FCSTD DOCUMENT  (FreeCAD 0.14R3702 (Git))
Label: Tantillus-MakeSpace
License: CC-BY 3.0
LicenseURL: http://creativecommons.org/licenses/by/3.0/
objects: Mesh::Feature×43, Part::Cylinder×43, Part::Cut×35, Part::Feature×18, App::DocumentObjectGroup×17, Part::MultiFuse×16, Part::FeaturePython×15, PartDesign::Pad×12, PartDesign::Chamfer×9, Sketcher::SketchObject×8, PartDesign::Pocket×7, Part::Box×5, Part::Sweep×3, Part::Chamfer×2, PartDesign::Revolution×2, Part::Helix×1
note: 197 computed .brp shape members not serialized (recipe doc carries the construction recipe); baked Part::Feature solids carry a one-line shape summary decoded from their .brp

FEATURE [PartDesign::Pad] Pad  label="Pata001"
  Length = 335
  Length2 = 100
  Placement = pos=(-110,-110,-167.5) rot=(0,0,1;0rad)
  Type = 0
FEATURE [PartDesign::Pad] Pad001  label="Pata002"
  Length = 335
  Length2 = 100
  Placement = pos=(110,-110,-167.5) rot=(0,0,1;0rad)
  Type = 0
FEATURE [PartDesign::Pad] Pad002  label="Pata003"
  Length = 335
  Length2 = 100
  Placement = pos=(-110,110,-167.5) rot=(0,0,1;0rad)
  Type = 0
FEATURE [PartDesign::Pad] Pad003  label="Pata004"
  Length = 335
  Length2 = 100
  Placement = pos=(110,110,-167.5) rot=(0,0,1;0rad)
  Type = 0
FEATURE [PartDesign::Pad] Pad004  label="Trab001"
  Length = 200
  Length2 = 100
  Placement = pos=(-100,-110,-157.5) rot=(0,1,0;1.5708rad)
  Type = 0
FEATURE [Mesh::Feature] panel_combine_BOTTOM
  Placement = pos=(-125,-125,-182.5) rot=(0.57735,0.57735,0.57735;2.0944rad)
FEATURE [PartDesign::Pad] Pad005  label="Trab002"
  Length = 200
  Length2 = 100
  Placement = pos=(-110,-100,-157.5) rot=(0.57735,-0.57735,-0.57735;4.18879rad)
  Type = 0
FEATURE [Mesh::Feature] panel_combine_BOTTOM001
  Placement = pos=(-125,125,-182.5) rot=(1,0,0;1.5708rad)
FEATURE [Mesh::Feature] panel_combine_BOTTOM002
  Placement = pos=(125,-125,-182.5) rot=(0,0.707107,0.707107;3.14159rad)
FEATURE [Mesh::Feature] panel_combine_BOTTOM003
  Placement = pos=(125,125,-182.5) rot=(0.57735,-0.57735,-0.57735;2.0944rad)
FEATURE [PartDesign::Pad] Pad006  label="Trab003"
  Length = 200
  Length2 = 100
  Placement = pos=(110,-100,-157.5) rot=(0.57735,-0.57735,-0.57735;4.18879rad)
  Type = 0
FEATURE [PartDesign::Pad] Pad007  label="Trab004"
  Length = 200
  Length2 = 100
  Placement = pos=(-100,110,-157.5) rot=(0,1,0;1.5708rad)
  Type = 0
FEATURE [PartDesign::Pad] Pad008  label="Trab005"
  Length = 200
  Length2 = 100
  Placement = pos=(-100,-110,157.5) rot=(0,1,0;1.5708rad)
  Type = 0
FEATURE [PartDesign::Pad] Pad009  label="Trab006"
  Length = 200
  Length2 = 100
  Placement = pos=(-110,-100,157.5) rot=(0.57735,-0.57735,-0.57735;4.18879rad)
  Type = 0
FEATURE [PartDesign::Pad] Pad010  label="Trab007"
  Length = 200
  Length2 = 100
  Placement = pos=(110,-100,157.5) rot=(0.57735,-0.57735,-0.57735;4.18879rad)
  Type = 0
FEATURE [PartDesign::Pad] Pad011  label="Trab008"
  Length = 200
  Length2 = 100
  Placement = pos=(-100,110,157.5) rot=(0,1,0;1.5708rad)
  Type = 0
FEATURE [Mesh::Feature] AnguloFrontDerecho
  Placement = pos=(136,-60,165.5) rot=(0.707107,-0.707107,0;3.14159rad)
FEATURE [Mesh::Feature] AnguloFrontIzquierdo
  Placement = pos=(-33,-60.5,163.5) rot=(0.707107,-0.707107,0;3.14159rad)
FEATURE [Mesh::Feature] AnguloTraseroDerecho  label="AnguloTraseroDer"
  Placement = pos=(33,60,163.5) rot=(0.707107,0.707107,0;3.14159rad)
FEATURE [Mesh::Feature] AnguloTraseroIzq
  Placement = pos=(-52,130,163.5) rot=(0.707107,-0.707107,0;3.14159rad)
FEATURE [App::DocumentObjectGroup] Grupo001  label="AngulosSup"
  Group = -> [AnguloFrontDerecho,AnguloFrontIzquierdo,AnguloTraseroDerecho,AnguloTraseroIzq]
FEATURE [App::DocumentObjectGroup] Grupo002  label="AngulosInf"
  Group = -> [panel_combine_BOTTOM,panel_combine_BOTTOM001,panel_combine_BOTTOM002,panel_combine_BOTTOM003]
FEATURE [PartDesign::Chamfer] Chamfer001
  Placement = pos=(-124,-80.5,128) rot=(0,0,1;1.5708rad)
  Size = 0.25
FEATURE [PartDesign::Chamfer] Chamfer
  Placement = pos=(124,-80.5,128) rot=(0,0,1;1.5708rad)
  Size = 0.25
FEATURE [PartDesign::Chamfer] Chamfer002
  Placement = pos=(124,80.5,128) rot=(0,0,1;1.5708rad)
  Size = 0.25
FEATURE [PartDesign::Chamfer] Chamfer003
  Placement = pos=(-124,80.5,128) rot=(0,0,1;1.5708rad)
  Size = 0.25
FEATURE [App::DocumentObjectGroup] Grupo003  label="rodamientosY"
  Group = -> [Chamfer001,Chamfer,Chamfer002,Chamfer003]
FEATURE [PartDesign::Chamfer] Chamfer004
  Placement = pos=(80.5,-124,108) rot=(0,0,1;3.14159rad)
  Size = 0.25
FEATURE [PartDesign::Chamfer] Chamfer005
  Placement = pos=(80.5,124.5,108) rot=(0,0,1;3.14159rad)
  Size = 0.25
FEATURE [PartDesign::Chamfer] Chamfer006
  Placement = pos=(-81,124.5,108) rot=(0,0,1;3.14159rad)
  Size = 0.25
FEATURE [PartDesign::Chamfer] Chamfer007
  Placement = pos=(-81,-124,108) rot=(0,0,1;3.14159rad)
  Size = 0.25
FEATURE [App::DocumentObjectGroup] Grupo004  label="rodamientosX"
  Group = -> [Chamfer004,Chamfer005,Chamfer006,Chamfer007]
FEATURE [PartDesign::Pocket] Pocket006
  Length = 3
  Type = 0
FEATURE [Part::FeaturePython] refine  label="motor"  # WARN: FeaturePython — macro-defined, semantics opaque (R4)
  Base = -> Pocket006
  Placement = pos=(212,80.5,128) rot=(0,-1,0;1.5708rad)
FEATURE [Part::Cylinder] Cylinder  label="Cilindro"
  Angle = 360
  Height = 40
  Placement = pos=(0,0,0) rot=(0,1,0;1.5708rad)
  Radius = 2.5
FEATURE [Part::Cylinder] Cylinder001  label="Cilindro001"
  Angle = 360
  Height = 44
  Placement = pos=(-2,0,0) rot=(0,1,0;1.5708rad)
  Radius = 1.5
FEATURE [Part::Cut] Cut  label="soporte1"
  Base = -> Cylinder
  Placement = pos=(125,65,143.5) rot=(0,0,1;0rad)
  Tool = -> Cylinder001
FEATURE [Part::Cylinder] Cylinder002  label="Cilindro002"
  Angle = 360
  Height = 40
  Placement = pos=(0,0,0) rot=(0,1,0;1.5708rad)
  Radius = 2.5
FEATURE [Part::Cylinder] Cylinder003  label="Cilindro003"
  Angle = 360
  Height = 44
  Placement = pos=(-2,0,0) rot=(0,1,0;1.5708rad)
  Radius = 1.5
FEATURE [Part::Cut] Cut001  label="soporte2"
  Base = -> Cylinder002
  Placement = pos=(125,96,143.5) rot=(0,0,1;0rad)
  Tool = -> Cylinder003
FEATURE [Part::Cylinder] Cylinder004  label="Cilindro004"
  Angle = 360
  Height = 40
  Placement = pos=(0,0,0) rot=(0,1,0;1.5708rad)
  Radius = 2.5
FEATURE [Part::Cylinder] Cylinder005  label="Cilindro005"
  Angle = 360
  Height = 44
  Placement = pos=(-2,0,0) rot=(0,1,0;1.5708rad)
  Radius = 1.5
FEATURE [Part::Cut] Cut002  label="soporte3"
  Base = -> Cylinder004
  Placement = pos=(125,65,112.5) rot=(0,0,1;0rad)
  Tool = -> Cylinder005
FEATURE [Part::Cylinder] Cylinder006  label="Cilindro006"
  Angle = 360
  Height = 40
  Placement = pos=(0,0,0) rot=(0,1,0;1.5708rad)
  Radius = 2.5
FEATURE [Part::Cylinder] Cylinder007  label="Cilindro007"
  Angle = 360
  Height = 44
  Placement = pos=(-2,0,0) rot=(0,1,0;1.5708rad)
  Radius = 1.5
FEATURE [Part::Cut] Cut003  label="soporte4"
  Base = -> Cylinder006
  Placement = pos=(125,96,112.5) rot=(0,0,1;0rad)
  Tool = -> Cylinder007
FEATURE [Part::Cylinder] Cylinder008  label="barraM8Ymotor"
  Angle = 360
  Height = 276
  Placement = pos=(-81,-138,108) rot=(-0.57735,0.57735,0.57735;2.0944rad)
  Radius = 4
FEATURE [Mesh::Feature] Ruedecilla
  Placement = pos=(-147,68,133.8) rot=(0,1,0;1.5708rad)
FEATURE [Part::Cut] Cut004  label="soporte005"
  Base = -> Cylinder004
  Placement = pos=(-65.5,125,92.5) rot=(0,0,1;1.5708rad)
  Tool = -> Cylinder005
FEATURE [Part::Cut] Cut005  label="soporte006"
  Base = -> Cylinder002
  Placement = pos=(-96.5,125,123.5) rot=(0,0,1;1.5708rad)
  Tool = -> Cylinder003
FEATURE [Part::Cut] Cut006  label="soporte007"
  Base = -> Cylinder
  Placement = pos=(-65.5,125,123.5) rot=(0,0,1;1.5708rad)
  Tool = -> Cylinder001
FEATURE [Part::FeaturePython] refine001  label="motor001"  # WARN: FeaturePython — macro-defined, semantics opaque (R4)
  Base = -> Pocket006
  Placement = pos=(-81,212,108) rot=(0.57735,-0.57735,0.57735;2.0944rad)
FEATURE [Part::Cut] Cut007  label="soporte008"
  Base = -> Cylinder006
  Placement = pos=(-96.5,125,92.5) rot=(0,0,1;1.5708rad)
  Tool = -> Cylinder007
FEATURE [Mesh::Feature] Ruedecilla001
  Placement = pos=(-68.5,-147,113.7) rot=(0.57735,-0.57735,-0.57735;4.18879rad)
FEATURE [Part::Cylinder] Cylinder009  label="barraM8Xmotor"
  Angle = 360
  Height = 276
  Placement = pos=(138,-80.5,128) rot=(0.707107,0,-0.707107;3.14159rad)
  Radius = 4
FEATURE [Part::Cylinder] Cylinder010  label="barraM8Y"
  Angle = 360
  Height = 276
  Placement = pos=(80.5,-138,108) rot=(-0.57735,0.57735,0.57735;2.0944rad)
  Radius = 4
FEATURE [Mesh::Feature] Ruedecilla002
  Placement = pos=(-147,-93,133.7) rot=(0,1,0;1.5708rad)
FEATURE [Part::Cylinder] Cylinder011  label="barraM8X"
  Angle = 360
  Height = 276
  Placement = pos=(138,80.5,128) rot=(0.707107,0,-0.707107;3.14159rad)
  Radius = 4
FEATURE [Mesh::Feature] Ruedecilla003
  Placement = pos=(93,-147,113.7) rot=(0.57735,-0.57735,-0.57735;4.18879rad)
FEATURE [Mesh::Feature] Ruedecilla004
  Placement = pos=(147,-93,122.3) rot=(0,-1,0;1.5708rad)
FEATURE [Mesh::Feature] Ruedecilla005
  Placement = pos=(93,147,102.3) rot=(0.57735,-0.57735,0.57735;2.0944rad)
FEATURE [Mesh::Feature] printable_lm8uu_v  label="printable-lm8uu1"
  Placement = pos=(7.9,0.3,115.1) rot=(1,0,0;1.5708rad)
FEATURE [Mesh::Feature] printable_lm8uu_v001  label="printable-lm8uu2"
  Placement = pos=(2,16.2,128.6) rot=(0,1,0;1.5708rad)
FEATURE [Part::Cylinder] Cylinder012  label="barraX"
  Angle = 360
  Height = 175
  Placement = pos=(-88,10,127) rot=(0,1,0;1.5708rad)
  Radius = 4
FEATURE [Part::Cylinder] Cylinder013  label="barraY"
  Angle = 360
  Height = 175
  Placement = pos=(9.5,87.3,108.9) rot=(1,0,0;1.5708rad)
  Radius = 4
FEATURE [Mesh::Feature] XY_end_left
  Placement = pos=(161.5,-113,87.5) rot=(0.57735,-0.57735,-0.57735;4.18879rad)
FEATURE [Mesh::Feature] XY_end_right
  Placement = pos=(0,20,-4.5) rot=(0,0,1;1.5708rad)
FEATURE [Mesh::Feature] printable_lm8uu_v002  label="printable-lm8uu003"
  Placement = pos=(78.9,15,114.3) rot=(1,0,0;1.5708rad)
FEATURE [Mesh::Feature] printable_lm8uu_v003  label="printable-lm8uu004"
  Placement = pos=(-82.6,16,114.2) rot=(1,0,0;1.5708rad)
FEATURE [Mesh::Feature] printable_lm8uu_v004  label="printable-lm8uu005"
  Placement = pos=(15.5,-82.1,121.8) rot=(0.57735,0.57735,-0.57735;4.18879rad)
FEATURE [Mesh::Feature] printable_lm8uu_v005  label="printable-lm8uu006"
  Placement = pos=(14.5,78.9,121.7) rot=(0.57735,0.57735,-0.57735;4.18879rad)
FEATURE [Mesh::Feature] XY_end_right001
  Placement = pos=(19.5,0.5,240.5) rot=(1,0,0;3.14159rad)
FEATURE [Mesh::Feature] XY_end_left001
  Placement = pos=(-113.5,161.5,148.5) rot=(0.707107,0,0.707107;3.14159rad)
FEATURE [App::DocumentObjectGroup] Grupo010  label="estremos"
  Group = -> [XY_end_left,XY_end_right,printable_lm8uu_v002,printable_lm8uu_v003,printable_lm8uu_v004,printable_lm8uu_v005,XY_end_right001,XY_end_left001]
FEATURE [Part::Cylinder] Cylinder014  label="barraM8008"
  Angle = 360
  Height = 225
  Placement = pos=(-33,79.3,-133.5) rot=(0,0,1;0rad)
  Radius = 4
FEATURE [Part::Cylinder] Cylinder015  label="barraM8009"
  Angle = 360
  Height = 225
  Placement = pos=(37,79.3,-133.5) rot=(0,0,1;0rad)
  Radius = 4
FEATURE [Mesh::Feature] Z_lift
  Placement = pos=(107,253.5,219.1) rot=(0,0,1;1.5708rad)
FEATURE [Mesh::Feature] printable_lm8uu_v007  label="printable-lm8uu-v004"
  Placement = pos=(35.3,85.5,-3.9) rot=(0,0,1;0rad)
FEATURE [Mesh::Feature] printable_lm8uu_v008  label="printable-lm8uu-v005"
  Placement = pos=(-34.6,85.5,-3.9) rot=(0,0,1;0rad)
FEATURE [Part::Box] Box  label="tablelisa"
  Height = 3
  Length = 120
  Placement = pos=(53,45,161) rot=(0,0,1;0rad)
  Width = 120
FEATURE [Part::FeaturePython] refine002  label="motor002"  # WARN: FeaturePython — macro-defined, semantics opaque (R4)
  Placement = pos=(2,79,-180.5) rot=(0,0,1;0rad)
FEATURE [Part::Cylinder] Cylinder016  label="Cilindro008"
  Angle = 360
  Height = 10
  Placement = pos=(79.5,114.1,158) rot=(0,0,1;0rad)
  Radius = 2.6
FEATURE [Part::Cylinder] Cylinder017  label="Cilindro009"
  Angle = 360
  Height = 10
  Placement = pos=(144.5,114.1,158) rot=(0,0,1;0rad)
  Radius = 2.6
FEATURE [Part::Cylinder] Cylinder018  label="Cilindro010"
  Angle = 360
  Height = 10
  Placement = pos=(144.5,152.1,158) rot=(0,0,1;0rad)
  Radius = 2.6
FEATURE [Part::Cylinder] Cylinder019  label="Cilindro011"
  Angle = 360
  Height = 10
  Placement = pos=(79.5,152.1,158) rot=(0,0,1;0rad)
  Radius = 2.6
FEATURE [Part::Cut] Cut008
  Base = -> Box
  Tool = -> Cylinder016
FEATURE [Part::Cut] Cut009
  Base = -> Cut008
  Tool = -> Cylinder017
FEATURE [Part::Cut] Cut010
  Base = -> Cut009
  Tool = -> Cylinder019
FEATURE [Part::Cut] Cut011  label="mesainf01"
  Base = -> Cut010
  Tool = -> Cylinder018
FEATURE [Part::Box] Box001  label="tablelisa001"
  Height = 3
  Length = 120
  Placement = pos=(53,45,174) rot=(0,0,1;0rad)
  Width = 120
FEATURE [Sketcher::SketchObject] Sketch
  Placement = pos=(53,45,177) rot=(0,0,1;0rad)
  Support = -> Box001 [Face6]
  sketch-geometry (3):
    g0: Circle CenterX=5 CenterY=5 CenterZ=0 NormalX=0 NormalY=0 NormalZ=1 Radius=1.5
    g1: Circle CenterX=115 CenterY=5 CenterZ=0 NormalX=0 NormalY=0 NormalZ=1 Radius=1.5
    g2: Circle CenterX=60 CenterY=105 CenterZ=0 NormalX=0 NormalY=0 NormalZ=1 Radius=1.5
  constraints (9):
    c: Equal(g2,g1)
    c: Equal(g1,g0)
    c: Radius(g0) = 1.5
    c: DistanceY(g-1,g0) = 5
    c: DistanceX(g-1,g0) = 5
    c: DistanceY(g-1,g1) = 5
    c: DistanceX(g-1,g1) = 115
    c: DistanceY(g-1,g2) = 105
    c: DistanceX(g-1,g2) = 60
FEATURE [PartDesign::Pocket] Pocket  label="mesasup"
  Length = 5
  Placement = pos=(53,45,174) rot=(0,0,1;0rad)
  Sketch = -> Sketch
  Type = 1
FEATURE [Sketcher::SketchObject] Sketch001
  ExternalGeometry = -> [Cut011]
  Placement = pos=(0,0,164) rot=(0,0,1;0rad)
  Support = -> Cut011 [Face3]
  sketch-geometry (3):
    g0: Circle CenterX=58 CenterY=50 CenterZ=0 NormalX=0 NormalY=0 NormalZ=1 Radius=1.5
    g1: Circle CenterX=168 CenterY=50 CenterZ=0 NormalX=0 NormalY=0 NormalZ=1 Radius=1.5
    g2: Circle CenterX=113 CenterY=150 CenterZ=0 NormalX=0 NormalY=0 NormalZ=1 Radius=1.5
  constraints (9):
    c: Equal(g2,g1)
    c: Equal(g1,g0)
    c: Radius(g1) = 1.5
    c: DistanceX(g0,g-4) = -5
    c: DistanceY(g0,g-4) = -5
    c: DistanceX(g1,g-4) = 5
    c: DistanceY(g1,g-4) = -5
    c: DistanceX(g2,g-3) = -60
    c: DistanceY(g2,g-3) = 15
FEATURE [PartDesign::Pocket] Pocket007  label="mesainf"
  Length = 5
  Sketch = -> Sketch001
  Type = 1
FEATURE [Part::Cylinder] Cylinder020  label="Cilindro012"
  Angle = 360
  Height = 22
  Radius = 1.5
FEATURE [Part::Chamfer] Chamfer008
  Base = -> Cylinder020
  Edges = 1 edges r=0.2: [Edge3]
FEATURE [Part::Cylinder] Cylinder021  label="Cilindro013"
  Angle = 360
  Height = 3
  Placement = pos=(0,0,21) rot=(0,0,1;0rad)
  Radius = 2
FEATURE [Part::Chamfer] Chamfer009
  Base = -> Cylinder021
  Edges = 1 edges r=0.2: [Edge1]
FEATURE [Part::MultiFuse] Fusion
  Shapes = -> [Chamfer008,Chamfer009]
FEATURE [Sketcher::SketchObject] Sketch002
  Placement = pos=(0,0,24) rot=(0,0,1;0rad)
  Support = -> Fusion [Face7]
  sketch-geometry (7):
    g0: LineSegment StartX=-1.25 StartY=0.721688 StartZ=0 EndX=0 EndY=1.44338 EndZ=0
    g1: LineSegment StartX=0 StartY=1.44338 StartZ=0 EndX=1.25 EndY=0.721688 EndZ=0
    g2: LineSegment StartX=1.25 StartY=0.721688 StartZ=0 EndX=1.25 EndY=-0.721688 EndZ=0
    g3: LineSegment StartX=1.25 StartY=-0.721688 StartZ=0 EndX=0 EndY=-1.44338 EndZ=0
    g4: LineSegment StartX=0 StartY=-1.44338 StartZ=0 EndX=-1.25 EndY=-0.721688 EndZ=0
    g5: LineSegment StartX=-1.25 StartY=-0.721688 StartZ=0 EndX=-1.25 EndY=0.721688 EndZ=0
    g6: LineSegment [constr] StartX=0 StartY=1.44338 StartZ=0 EndX=0 EndY=0 EndZ=0
  constraints (20):
    c: PointOnObject(g0,g-2)
    c: Coincident(g0,g1)
    c: Coincident(g1,g2)
    c: Vertical(g2)
    c: Coincident(g2,g3)
    c: PointOnObject(g3,g-2)
    c: Coincident(g3,g4)
    c: Coincident(g4,g5)
    c: Coincident(g5,g0)
    c: Vertical(g5)
    c: Equal(g5,g0)
    c: Equal(g0,g1)
    c: Equal(g1,g2)
    c: Equal(g2,g3)
    c: Equal(g3,g4)
    c: Coincident(g6,g0)
    c: Coincident(g6,g-1)
    c: Angle(g0,g6) = 1.0472
    c: Symmetric(g0,g3,g-1)
    c: DistanceX(g2,g4) = -2.5
FEATURE [PartDesign::Pocket] Pocket008
  Length = 2
  Sketch = -> Sketch002
  Type = 0
FEATURE [Part::Cylinder] Cylinder022  label="Cilindro014"
  Angle = 360
  Height = 0.3
  Placement = pos=(0,0,20.7) rot=(0,0,1;0rad)
  Radius = 3
FEATURE [Part::MultiFuse] Fusion001
  Shapes = -> [Cylinder022,Pocket008]
FEATURE [Part::Cylinder] Cylinder023  label="Cilindro015"
  Angle = 360
  Height = 0.3
  Placement = pos=(0,0,17.4) rot=(0,0,1;0rad)
  Radius = 3
FEATURE [Part::MultiFuse] Fusion002
  Shapes = -> [Cylinder023,Fusion001]
FEATURE [Part::Cylinder] Cylinder024  label="Cilindro016"
  Angle = 360
  Height = 0.3
  Placement = pos=(0,0,7.7) rot=(0,0,1;0rad)
  Radius = 3
FEATURE [Part::MultiFuse] Fusion003
  Shapes = -> [Cylinder024,Fusion002]
FEATURE [Part::Cylinder] Cylinder025  label="Cilindro017"
  Angle = 360
  Height = 0.3
  Placement = pos=(0,0,4.4) rot=(0,0,1;0rad)
  Radius = 3
FEATURE [Part::MultiFuse] Fusion004
  Shapes = -> [Fusion003,Cylinder025]
FEATURE [Part::Helix] Helix  label="Muelletrazo"
  Angle = 0
  Height = 9.4
  LocalCoord = 0
  Pitch = 1
  Placement = pos=(0,0,8) rot=(0,0,1;0rad)
  Radius = 2.5
  Style = 1
FEATURE [Sketcher::SketchObject] Sketch003
  Placement = pos=(0,0,0) rot=(1,0,0;1.5708rad)
  sketch-geometry (1):
    g0: Circle CenterX=2.5 CenterY=8 CenterZ=0 NormalX=0 NormalY=0 NormalZ=1 Radius=0.1
  constraints (3):
    c: Radius(g0) = 0.1
    c: DistanceX(g-1,g0) = 2.5
    c: DistanceY(g-1,g0) = 8
FEATURE [Part::Sweep] Sweep
  Frenet = true
  Sections = -> [Sketch003]
  Solid = true
  Spine = -> Helix [Edge1]
  Transition = 1
FEATURE [Part::MultiFuse] Fusion005  label="tonillocama"
  Placement = pos=(-52,-59,-11) rot=(0,0,1;0rad)
  Shapes = -> [Fusion004,Sweep]
FEATURE [Part::Sweep] Sweep001
  Frenet = true
  Sections = -> [Sketch003]
  Solid = true
  Spine = -> Helix [Edge1]
  Transition = 1
FEATURE [Part::MultiFuse] Fusion006
  Shapes = -> [Fusion003,Cylinder025]
FEATURE [Part::MultiFuse] Fusion007  label="tonillocama001"
  Placement = pos=(58,-59,-11) rot=(0,0,1;0rad)
  Shapes = -> [Fusion006,Sweep001]
FEATURE [Part::MultiFuse] Fusion008
  Shapes = -> [Fusion003,Cylinder025]
FEATURE [Part::Sweep] Sweep002
  Frenet = true
  Sections = -> [Sketch003]
  Solid = true
  Spine = -> Helix [Edge1]
  Transition = 1
FEATURE [Part::MultiFuse] Fusion009  label="tonillocama002"
  Placement = pos=(3,41,-11) rot=(0,0,1;0rad)
  Shapes = -> [Fusion008,Sweep002]
FEATURE [Part::Cylinder] Cylinder026  label="Cilindro018"
  Angle = 360
  Height = 3
  Radius = 7
FEATURE [Sketcher::SketchObject] Sketch004  label="PasoTuerca"
  Placement = pos=(0,0,3) rot=(0,0,1;0rad)
  Support = -> Cylinder026 [Face2]
  sketch-geometry (8):
    g0: LineSegment StartX=-3.46409 StartY=0 StartZ=0 EndX=-1.73205 EndY=3 EndZ=0
    g1: LineSegment StartX=-1.73205 StartY=3 StartZ=0 EndX=1.73205 EndY=3 EndZ=0
    g2: LineSegment StartX=1.73205 StartY=3 StartZ=0 EndX=3.46409 EndY=0 EndZ=0
    g3: LineSegment StartX=3.46409 StartY=0 StartZ=0 EndX=1.73205 EndY=-3 EndZ=0
    g4: LineSegment StartX=1.73205 StartY=-3 StartZ=0 EndX=-1.73205 EndY=-3 EndZ=0
    g5: LineSegment StartX=-1.73205 StartY=-3 StartZ=0 EndX=-3.46409 EndY=0 EndZ=0
    g6: LineSegment [constr] StartX=-3.46409 StartY=0 StartZ=0 EndX=0 EndY=0 EndZ=0
    g7: LineSegment [constr] StartX=-1.73205 StartY=3 StartZ=0 EndX=0 EndY=0 EndZ=0
  constraints (21):
    c: Coincident(g0,g1)
    c: Coincident(g1,g2)
    c: Coincident(g2,g3)
    c: Coincident(g3,g4)
    c: Coincident(g4,g5)
    c: Coincident(g5,g0)
    c: Equal(g5,g0)
    c: Equal(g0,g1)
    c: Equal(g1,g2)
    c: Equal(g2,g3)
    c: Equal(g3,g4)
    c: Coincident(g6,g0)
    c: Horizontal(g1)
    c: Horizontal(g4)
    c: DistanceY(g0,g4) = -6
    c: Symmetric(g4,g0,g6)
    c: Symmetric(g0,g2,g6)
    c: Coincident(g7,g0)
    c: Coincident(g7,g6)
    c: Angle(g7,g6) = 1.0472
    c: Coincident(g6,g-1)
FEATURE [PartDesign::Pocket] Pocket009
  Length = 2
  Sketch = -> Sketch004
  Type = 0
FEATURE [PartDesign::Chamfer] Chamfer010
  Base = -> Pocket009 [Edge1]
  Size = 1
FEATURE [Part::Cylinder] Cylinder027  label="Cilindro019"
  Angle = 360
  Height = 10
  Placement = pos=(0,0,-2) rot=(0,0,1;0rad)
  Radius = 1.5
FEATURE [Part::Cut] Cut012
  Base = -> Chamfer010
  Tool = -> Cylinder027
FEATURE [Part::Cylinder] Cylinder028  label="Cilindro020"
  Angle = 360
  Height = 10
  Placement = pos=(7,0,-2) rot=(0,0,1;0rad)
  Radius = 1
FEATURE [Part::FeaturePython] Array  # Draft array (typed FeaturePython)
  Angle = 360
  ArrayType = 1
  Axis = (0,0,1)
  Base = -> Cylinder028
  Center = (0,0,0)
  IntervalX = (1,0,0)
  IntervalY = (0,1,0)
  IntervalZ = (0,0,1)
  NumberPolar = 12
  NumberX = 2
  NumberY = 2
  NumberZ = 1
FEATURE [Part::Cut] Cut013
  Base = -> Cut012
  Placement = pos=(-52,-59,-10.3) rot=(0,0,1;0rad)
  Tool = -> Array
FEATURE [Part::Cut] Cut014
  Base = -> Chamfer010
  Tool = -> Cylinder027
FEATURE [Part::FeaturePython] Array001  # Draft array (typed FeaturePython)
  Angle = 360
  ArrayType = 1
  Axis = (0,0,1)
  Base = -> Cylinder028
  Center = (0,0,0)
  IntervalX = (1,0,0)
  IntervalY = (0,1,0)
  IntervalZ = (0,0,1)
  NumberPolar = 12
  NumberX = 2
  NumberY = 2
  NumberZ = 1
FEATURE [Part::Cut] Cut015
  Base = -> Cut014
  Placement = pos=(58,-59,-10.3) rot=(0,0,1;0rad)
  Tool = -> Array001
FEATURE [Part::Cut] Cut016
  Base = -> Chamfer010
  Tool = -> Cylinder027
FEATURE [Part::FeaturePython] Array002  # Draft array (typed FeaturePython)
  Angle = 360
  ArrayType = 1
  Axis = (0,0,1)
  Base = -> Cylinder028
  Center = (0,0,0)
  IntervalX = (1,0,0)
  IntervalY = (0,1,0)
  IntervalZ = (0,0,1)
  NumberPolar = 12
  NumberX = 2
  NumberY = 2
  NumberZ = 1
FEATURE [Part::Cut] Cut017
  Base = -> Cut016
  Placement = pos=(3,41,-10.3) rot=(0,0,1;0rad)
  Tool = -> Array002
FEATURE [Part::Box] Box002  label="metraquilato"
  Height = 5
  Length = 125
  Placement = pos=(-59.5,-66.5,9.8) rot=(0,0,1;0rad)
  Width = 125
FEATURE [Part::Cylinder] Cylinder029  label="Cilindro021"
  Angle = 360
  Height = 40
  Radius = 8
FEATURE [Part::Cylinder] Cylinder030  label="Cilindro022"
  Angle = 360
  Height = 4.6
  Radius = 8
FEATURE [Part::Cylinder] Cylinder031  label="Cilindro023"
  Angle = 360
  Height = 10
  Placement = pos=(0,0,-2) rot=(0,0,1;0rad)
  Radius = 6
FEATURE [Part::Cut] Cut018
  Base = -> Cylinder030
  Placement = pos=(0,0,30.6) rot=(0,0,1;0rad)
  Tool = -> Cylinder031
FEATURE [Part::Cut] Cut019
  Base = -> Cylinder029
  Tool = -> Cut018
FEATURE [Part::Cylinder] Cylinder032  label="Cilindro024"
  Angle = 360
  Height = 42
  Placement = pos=(0,0,-1) rot=(0,0,1;0rad)
  Radius = 3.25
FEATURE [Part::Cut] Cut020
  Base = -> Cut019
  Tool = -> Cylinder032
FEATURE [Part::Cylinder] Cylinder033  label="Cilindro025"
  Angle = 360
  Height = 4.2
  Placement = pos=(0,0,-1) rot=(0,0,1;0rad)
  Radius = 4
FEATURE [Sketcher::SketchObject] Sketch005
  Placement = pos=(0,0,0) rot=(1,0,0;1.5708rad)
  sketch-geometry (4):
    g0: LineSegment [constr] StartX=-5 StartY=0 StartZ=0 EndX=5 EndY=0 EndZ=0
    g1: LineSegment StartX=-11.6906 StartY=3.86281 StartZ=0 EndX=-1.29847 EndY=-2.13708 EndZ=0
    g2: LineSegment StartX=-11.6906 StartY=-2.13708 StartZ=0 EndX=-11.6906 EndY=3.86281 EndZ=0
    g3: LineSegment StartX=-11.6906 StartY=-2.13708 StartZ=0 EndX=-1.29847 EndY=-2.13708 EndZ=0
  constraints (11):
    c: PointOnObject(g0,g-1)
    c: PointOnObject(g0,g-1)
    c: DistanceX(g0,g0) = -10
    c: Coincident(g2,g1)
    c: Vertical(g2)
    c: PointOnObject(g0,g1)
    c: Symmetric(g0,g0,g-2)
    c: Coincident(g3,g2)
    c: Coincident(g3,g1)
    c: Horizontal(g3)
    c: Angle(g0,g1) = 2.61799
FEATURE [Part::Cut] Cut021
  Base = -> Cut020
  Tool = -> Cylinder033
FEATURE [PartDesign::Revolution] Revolution
  Angle = 360
  Axis = (0,0,1)
  Base = (0,0,0)
  Placement = pos=(0,0,0) rot=(1,0,0;1.5708rad)
  ReferenceAxis = -> Sketch005 [V_Axis]
  Sketch = -> Sketch005
FEATURE [Part::Cut] Cut022
  Base = -> Cut021
  Tool = -> Revolution
FEATURE [Part::Cylinder] Cylinder034  label="Cilindro026"
  Angle = 360
  Height = 10
  Placement = pos=(4.2,0,0) rot=(0,1,0;1.5708rad)
  Radius = 1
FEATURE [Part::Cylinder] Cylinder035  label="Cilindro027"
  Angle = 360
  Height = 2
  Placement = pos=(0,0,-1) rot=(0,0,1;0rad)
  Radius = 4.2
FEATURE [Part::Cylinder] Cylinder036  label="Cilindro028"
  Angle = 60
  Height = 2
  Placement = pos=(0,0,-1) rot=(0,0,1;0rad)
  Radius = 14.2
FEATURE [Part::Cut] Cut023
  Base = -> Cylinder036
  Tool = -> Cylinder035
FEATURE [Part::Cylinder] Cylinder037  label="Cilindro029"
  Angle = 360
  Height = 10
  Placement = pos=(2.1,3.63731,0) rot=(-0.447214,0.774597,0.447214;1.82348rad)
  Radius = 1
FEATURE [Part::MultiFuse] Fusion010
  Shapes = -> [Cylinder034,Cut023]
FEATURE [Part::MultiFuse] Fusion011
  Shapes = -> [Cylinder037,Fusion010]
FEATURE [Part::FeaturePython] Array003  # Draft array (typed FeaturePython)
  Angle = 360
  ArrayType = 1
  Axis = (0,0,1)
  Base = -> Fusion011
  Center = (0,0,0)
  IntervalX = (1,0,0)
  IntervalY = (0,1,0)
  IntervalZ = (0,0,1)
  NumberPolar = 4
  NumberX = 1
  NumberY = 1
  NumberZ = 1
  Placement = pos=(0,0,13.5) rot=(0,0,1;0.261799rad)
FEATURE [Part::MultiFuse] Fusion012
  Shapes = -> [Cylinder037,Fusion010]
FEATURE [Part::FeaturePython] Array004  # Draft array (typed FeaturePython)
  Angle = 360
  ArrayType = 1
  Axis = (0,0,1)
  Base = -> Fusion012
  Center = (0,0,0)
  IntervalX = (1,0,0)
  IntervalY = (0,1,0)
  IntervalZ = (0,0,1)
  NumberPolar = 4
  NumberX = 1
  NumberY = 1
  NumberZ = 1
  Placement = pos=(0,0,16.5) rot=(0,0,1;0.261799rad)
FEATURE [Part::FeaturePython] Array005  # Draft array (typed FeaturePython)
  Angle = 360
  ArrayType = 1
  Axis = (0,0,1)
  Base = -> Fusion011
  Center = (0,0,0)
  IntervalX = (1,0,0)
  IntervalY = (0,1,0)
  IntervalZ = (0,0,1)
  NumberPolar = 4
  NumberX = 1
  NumberY = 1
  NumberZ = 1
  Placement = pos=(0,0,22.5) rot=(0,0,1;0.261799rad)
FEATURE [Part::MultiFuse] Fusion013
  Shapes = -> [Cylinder037,Fusion010]
FEATURE [Part::FeaturePython] Array006  # Draft array (typed FeaturePython)
  Angle = 360
  ArrayType = 1
  Axis = (0,0,1)
  Base = -> Fusion013
  Center = (0,0,0)
  IntervalX = (1,0,0)
  IntervalY = (0,1,0)
  IntervalZ = (0,0,1)
  NumberPolar = 4
  NumberX = 1
  NumberY = 1
  NumberZ = 1
  Placement = pos=(0,0,19.5) rot=(0,0,1;0.261799rad)
FEATURE [Part::MultiFuse] Fusion014
  Shapes = -> [Cylinder037,Fusion010]
FEATURE [Part::FeaturePython] Array007  # Draft array (typed FeaturePython)
  Angle = 360
  ArrayType = 1
  Axis = (0,0,1)
  Base = -> Fusion014
  Center = (0,0,0)
  IntervalX = (1,0,0)
  IntervalY = (0,1,0)
  IntervalZ = (0,0,1)
  NumberPolar = 4
  NumberX = 1
  NumberY = 1
  NumberZ = 1
  Placement = pos=(0,0,25.5) rot=(0,0,1;0.261799rad)
FEATURE [Part::Box] Box003  label="Cubo"
  Height = 8
  Length = 3
  Placement = pos=(6.5,-10,0) rot=(0,0,1;0rad)
  Width = 20
FEATURE [Part::Box] Box004  label="Cubo001"
  Height = 8
  Length = 3
  Placement = pos=(-9.5,-10,0) rot=(0,0,1;0rad)
  Width = 20
FEATURE [Part::Cut] Cut024
  Base = -> Cut022
  Tool = -> Box003
FEATURE [Part::Cut] Cut025
  Base = -> Cut024
  Tool = -> Box004
FEATURE [Part::Cut] Cut026
  Base = -> Cut025
  Tool = -> Array003
FEATURE [Part::Cut] Cut027
  Base = -> Cut026
  Tool = -> Array004
FEATURE [Part::Cut] Cut028
  Base = -> Cut027
  Tool = -> Array007
FEATURE [Part::Cut] Cut029
  Base = -> Cut028
  Tool = -> Array006
FEATURE [Part::Cut] Cut030
  Base = -> Cut029
  Tool = -> Array005
FEATURE [Part::Cylinder] Cylinder038  label="Cilindro030"
  Angle = 360
  Height = 2
  Placement = pos=(-1,5.2,16.5) rot=(0,1,0;1.5708rad)
  Radius = 1
FEATURE [Part::FeaturePython] Array008  # Draft array (typed FeaturePython)
  Angle = 360
  ArrayType = 1
  Axis = (0,0,1)
  Base = -> Cylinder038
  Center = (0,0,0)
  IntervalX = (1,0,0)
  IntervalY = (0,1,0)
  IntervalZ = (0,0,1)
  NumberPolar = 4
  NumberX = 0
  NumberY = 0
  NumberZ = 0
FEATURE [Part::Cylinder] Cylinder039  label="Cilindro031"
  Angle = 360
  Height = 2
  Placement = pos=(-1,5.2,16.5) rot=(0,1,0;1.5708rad)
  Radius = 1
FEATURE [Part::FeaturePython] Array009  # Draft array (typed FeaturePython)
  Angle = 360
  ArrayType = 1
  Axis = (0,0,1)
  Base = -> Cylinder039
  Center = (0,0,0)
  IntervalX = (1,0,0)
  IntervalY = (0,1,0)
  IntervalZ = (0,0,1)
  NumberPolar = 4
  NumberX = 0
  NumberY = 0
  NumberZ = 0
  Placement = pos=(0,0,3) rot=(0,0,1;0rad)
FEATURE [Part::Cylinder] Cylinder040  label="Cilindro032"
  Angle = 360
  Height = 2
  Placement = pos=(-1,5.2,16.5) rot=(0,1,0;1.5708rad)
  Radius = 1
FEATURE [Part::FeaturePython] Array010  # Draft array (typed FeaturePython)
  Angle = 360
  ArrayType = 1
  Axis = (0,0,1)
  Base = -> Cylinder040
  Center = (0,0,0)
  IntervalX = (1,0,0)
  IntervalY = (0,1,0)
  IntervalZ = (0,0,1)
  NumberPolar = 4
  NumberX = 0
  NumberY = 0
  NumberZ = 0
  Placement = pos=(0,0,6) rot=(0,0,1;0rad)
FEATURE [Part::Cylinder] Cylinder041  label="Cilindro033"
  Angle = 360
  Height = 2
  Placement = pos=(-1,5.2,16.5) rot=(0,1,0;1.5708rad)
  Radius = 1
FEATURE [Part::FeaturePython] Array011  # Draft array (typed FeaturePython)
  Angle = 360
  ArrayType = 1
  Axis = (0,0,1)
  Base = -> Cylinder041
  Center = (0,0,0)
  IntervalX = (1,0,0)
  IntervalY = (0,1,0)
  IntervalZ = (0,0,1)
  NumberPolar = 4
  NumberX = 0
  NumberY = 0
  NumberZ = 0
  Placement = pos=(0,0,9) rot=(0,0,1;0rad)
FEATURE [Part::Cut] Cut031
  Base = -> Cut030
  Tool = -> Array008
FEATURE [Part::Cut] Cut032
  Base = -> Cut031
  Tool = -> Array009
FEATURE [Part::Cut] Cut033
  Base = -> Cut032
  Tool = -> Array010
FEATURE [Part::Cut] Cut034  label="cuerpo j-head"
  Base = -> Cut033
  Placement = pos=(-9.8,-10.3,77.5) rot=(0,0,-1;1.5708rad)
  Tool = -> Array011
FEATURE [Sketcher::SketchObject] Sketch006
  Placement = pos=(12.7,0,0) rot=(0.57735,0.57735,0.57735;2.0944rad)
  sketch-geometry (1):
    g0: Circle CenterX=12.1 CenterY=4.1 CenterZ=0 NormalX=0 NormalY=0 NormalZ=1 Radius=3
  constraints (1):
    c: Radius(g0) = 3
FEATURE [PartDesign::Pocket] Pocket010
  Length = 5
  Sketch = -> Sketch006
  Type = 1
FEATURE [PartDesign::Revolution] Revolution001
  Angle = 360
  Axis = (0,0,1)
  Base = (0,0,0)
  Placement = pos=(6.35,5,0) rot=(1,0,0;1.5708rad)
FEATURE [Part::MultiFuse] Fusion015  label="hotend"
  Placement = pos=(-14.8,-3.8,68.5) rot=(0,0,-1;1.5708rad)
  Shapes = -> [Pocket010,Revolution001]
FEATURE [App::DocumentObjectGroup] Grupo014  label="J-Head"
  Group = -> [Fusion015,Cut034]
FEATURE [Mesh::Feature] carro_hotend  label="carro-hotend"
  Placement = pos=(-1.2,-0.3,100.2) rot=(0,0,1;0rad)
FEATURE [Mesh::Feature] Endstop_holder
  Placement = pos=(-5.9,161.5,121.5) rot=(0.707107,0.707107,0;3.14159rad)
FEATURE [Mesh::Feature] plataforma_cama  label="plataforma-cama"
  Placement = pos=(2,79,-14.5) rot=(0,0,-1;1.5708rad)
FEATURE [Mesh::Feature] z_lower_bracket20
  Placement = pos=(2,79,-128.5) rot=(0.707107,0.707107,0;3.14159rad)
FEATURE [Mesh::Feature] z_upper_bracket_tornillosextra_525zz  label="z_upper-bracket-tornillosextra-525zz"
  Placement = pos=(2,79,89.5) rot=(0.707107,0.707107,0;3.14159rad)
FEATURE [Part::Feature] Pad012001  label="Trab009"
  Placement = pos=(-110,-110,-160.5) rot=(0,0,1;0rad)
  shape: bbox 200 x 20 x 20 mm, 51 faces (baked)
FEATURE [App::DocumentObjectGroup] Grupo  label="T-Slot"
  Group = -> [Pad006,Pad007,Pad008,Pad009,Pad010,Pad011,Pad005,Pad,Pad001,Pad002,Pad003,Pad004,Pad012001]
FEATURE [Part::Feature] Pocket007001  label="mesainf002"
  Placement = pos=(0,-5,0.2) rot=(0,0,1;0rad)
  shape: bbox 120 x 120 x 3 mm, 13 faces (baked)
FEATURE [Part::Feature] Pocket007002  label="mesasup001"
  Placement = pos=(-110,-109,-167.3) rot=(0,0,1;0rad)
  shape: bbox 120 x 120 x 3 mm, 9 faces (baked)
FEATURE [Sketcher::SketchObject] Sketch007
  Placement = pos=(0,-5,161.2) rot=(1,0,0;3.14159rad)
  Support = -> Pocket007001 [Face5]
  sketch-geometry (4):
    g0: Circle CenterX=92.0359 CenterY=-98.0016 CenterZ=0 NormalX=0 NormalY=0 NormalZ=1 Radius=3
    g1: Circle CenterX=131.948 CenterY=-98.0016 CenterZ=0 NormalX=0 NormalY=0 NormalZ=1 Radius=3
    g2: Circle CenterX=92.0359 CenterY=-148.05 CenterZ=0 NormalX=0 NormalY=0 NormalZ=1 Radius=3
    g3: Circle CenterX=131.948 CenterY=-148.05 CenterZ=0 NormalX=0 NormalY=0 NormalZ=1 Radius=3
  constraints (4):
    c: Radius(g0) = 3
    c: Equal(g0,g1)
    c: Equal(g1,g3)
    c: Equal(g3,g2)
FEATURE [PartDesign::Pocket] Pocket007003  label="mesainf003"
  Length = 5
  Placement = pos=(0,-5,0.2) rot=(0,0,1;0rad)
  Sketch = -> Sketch007
  Type = 1
FEATURE [App::DocumentObjectGroup] Grupo013  label="ocultar"
  Group = -> [Box,Z_lift,Box001,Cut011,Fusion,Helix,Pocket009,Cylinder026,Pocket,Pocket007,Pocket007001,Pocket007003]
FEATURE [Part::Feature] Pocket007003001  label="mesainf004"
  Placement = pos=(-110,-104,-167.5) rot=(0,0,1;0rad)
  shape: bbox 120 x 120 x 3 mm, 17 faces (baked)
FEATURE [Part::Cylinder] Cylinder042  label="VarillaRoscada"
  Angle = 360
  Height = 205
  Placement = pos=(2,79,-106.5) rot=(0,0,1;0rad)
  Radius = 2.5
FEATURE [Mesh::Feature] spectra_reel_m  label="spectra-reel-m8"
  Placement = pos=(-42,80.5,128) rot=(0.57735,0.57735,-0.57735;4.18879rad)
FEATURE [Mesh::Feature] spectra_reel_m001  label="spectra-reel-m009"
  Placement = pos=(-81,-42,108) rot=(0.57735,-0.57735,0.57735;2.0944rad)
FEATURE [Mesh::Feature] spectra_reel_m002  label="spectra-reel-m010"
  Placement = pos=(80.5,-42,108) rot=(0.57735,-0.57735,0.57735;2.0944rad)
FEATURE [Mesh::Feature] spectra_reel_m003  label="spectra-reel-m011"
  Placement = pos=(-81,42,108) rot=(0.57735,-0.57735,-0.57735;4.18879rad)
FEATURE [Mesh::Feature] spectra_reel_m004  label="spectra-reel-m012"
  Placement = pos=(80.5,42,108) rot=(0.57735,-0.57735,-0.57735;4.18879rad)
FEATURE [Mesh::Feature] spectra_reel_m005  label="spectra-reel-m013"
  Placement = pos=(42,-80.5,128) rot=(0.57735,0.57735,0.57735;2.0944rad)
FEATURE [Mesh::Feature] spectra_reel_m006  label="spectra-reel-m014"
  Placement = pos=(42,80.5,128) rot=(0.57735,0.57735,0.57735;2.0944rad)
FEATURE [Mesh::Feature] spectra_reel_m007  label="spectra-reel-m015"
  Placement = pos=(-42,-80.5,128) rot=(0.57735,0.57735,-0.57735;4.18879rad)
FEATURE [App::DocumentObjectGroup] Grupo006  label="barras"
  Group = -> [Cylinder008,Ruedecilla,Cylinder009,Ruedecilla001,Cylinder010,Ruedecilla002,Cylinder011,Ruedecilla003,Ruedecilla004,Ruedecilla005,spectra_reel_m,spectra_reel_m001,spectra_reel_m002,spectra_reel_m003,spectra_reel_m004,spectra_reel_m005,spectra_reel_m006,spectra_reel_m007]
FEATURE [Mesh::Feature] coupler
  Placement = pos=(2,79,-123) rot=(0,0,1;0rad)
FEATURE [Part::Feature] Part__Feature  label="ParteBaja"
  Placement = pos=(28,76.5,53) rot=(0,1,0;3.14159rad)
  shape: bbox 12.6 x 5.8 x 3 mm, 26 faces (baked)
FEATURE [Part::Feature] Part__Feature001  label="ParteBaja001"
  Placement = pos=(28,76.5,53) rot=(0,1,0;3.14159rad)
  shape: bbox 2.5 x 5.8 x 1 mm, 6 faces (baked)
FEATURE [Part::Feature] Part__Feature002  label="ParteAlta"
  Placement = pos=(28,76.5,53) rot=(0,1,0;3.14159rad)
  shape: bbox 12.6 x 5.8 x 5.4 mm, 16 faces (baked)
FEATURE [Part::Feature] Part__Feature003  label="Pletina"
  Placement = pos=(28,76.5,53) rot=(0,1,0;3.14159rad)
  shape: bbox 11.62 x 4 x 3.299 mm, 14 faces (baked)
FEATURE [Part::Feature] Part__Feature004  label="Cubo007"
  Placement = pos=(28,76.5,53) rot=(0,1,0;3.14159rad)
  shape: bbox 2 x 2 x 1 mm, 6 faces (baked)
FEATURE [Part::Feature] Part__Feature005  label="GND"
  Placement = pos=(28,76.5,53) rot=(0,1,0;3.14159rad)
  shape: bbox 0.4 x 0.4 x 4 mm, 3 faces (baked)
FEATURE [Part::Feature] Part__Feature006  label="NC"
  Placement = pos=(28,76.5,53) rot=(0,1,0;3.14159rad)
  shape: bbox 0.4 x 0.4 x 4 mm, 3 faces (baked)
FEATURE [Part::Feature] Part__Feature007  label="NO"
  Placement = pos=(28,76.5,53) rot=(0,1,0;3.14159rad)
  shape: bbox 0.4 x 0.4 x 4 mm, 3 faces (baked)
FEATURE [App::DocumentObjectGroup] Grupo015  label="endstop1"
  Group = -> [Part__Feature,Part__Feature001,Part__Feature002,Part__Feature003,Part__Feature004,Part__Feature005,Part__Feature006,Part__Feature007]
FEATURE [App::DocumentObjectGroup] Grupo011  label="EjeZ"
  Group = -> [Cylinder014,Cylinder015,printable_lm8uu_v007,printable_lm8uu_v008,refine002,Fusion005,Fusion007,Fusion009,Cut013,Cut015,Cut017,Box002,Endstop_holder,plataforma_cama,z_lower_bracket20,z_upper_bracket_tornillosextra_525zz,Pocket007002,Pocket007003001,Cylinder042,coupler,Grupo015]
FEATURE [Mesh::Feature] coupler001
  Placement = pos=(-81,161,108) rot=(1,0,0;1.5708rad)
FEATURE [App::DocumentObjectGroup] Grupo007  label="motor eje X"
  Group = -> [refine001,Cut006,Cut005,Cut004,Cut007,coupler001]
FEATURE [Mesh::Feature] coupler002
  Placement = pos=(131,80.5,128) rot=(0,1,0;1.5708rad)
FEATURE [App::DocumentObjectGroup] Grupo005  label="motor eje Y"
  Group = -> [refine,Cut,Cut001,Cut002,Cut003,coupler002]
FEATURE [Part::Feature] Part__Feature008  label="Inferior"
  Placement = pos=(-19,16,108) rot=(0,-0.707107,0.707107;3.14159rad)
  shape: bbox 10.5 x 6.5 x 20 mm, 37 faces (baked)
FEATURE [Part::Feature] Part__Feature009  label="Superior"
  Placement = pos=(-19,16,108) rot=(0,-0.707107,0.707107;3.14159rad)
  shape: bbox 14 x 6.5 x 20 mm, 19 faces (baked)
FEATURE [Part::Feature] Part__Feature010  label="Pesta?a001"
  Placement = pos=(-19,16,108) rot=(0,-0.707107,0.707107;3.14159rad)
  shape: bbox 8.605 x 4 x 20.99 mm, 10 faces (baked)
FEATURE [App::DocumentObjectGroup] Grupo016  label="endstop2"
  Group = -> [Part__Feature008,Part__Feature009,Part__Feature010]
FEATURE [Part::Feature] Part__Feature011  label="Pesta?a002"
  Placement = pos=(16,-19.2,127.3) rot=(0.57735,-0.57735,-0.57735;2.0944rad)
  shape: bbox 4 x 8.605 x 20.99 mm, 10 faces (baked)
FEATURE [Part::Feature] Part__Feature012  label="Superior001"
  Placement = pos=(16,-19.2,127.3) rot=(0.57735,-0.57735,-0.57735;2.0944rad)
  shape: bbox 6.5 x 14 x 20 mm, 19 faces (baked)
FEATURE [Part::Feature] Part__Feature013  label="Inferior001"
  Placement = pos=(16,-19.2,127.3) rot=(0.57735,-0.57735,-0.57735;2.0944rad)
  shape: bbox 6.5 x 10.5 x 20 mm, 37 faces (baked)
FEATURE [App::DocumentObjectGroup] Grupo017  label="endstop003"
  Group = -> [Part__Feature013,Part__Feature012,Part__Feature011]
FEATURE [App::DocumentObjectGroup] Grupo009  label="carro"
  Group = -> [printable_lm8uu_v,printable_lm8uu_v001,Cylinder012,Cylinder013,carro_hotend,Grupo016,Grupo017]
FEATURE [App::DocumentObjectGroup] Grupo008  label="EjeXY"
  Group = -> [Grupo009,Grupo010,Grupo014]
